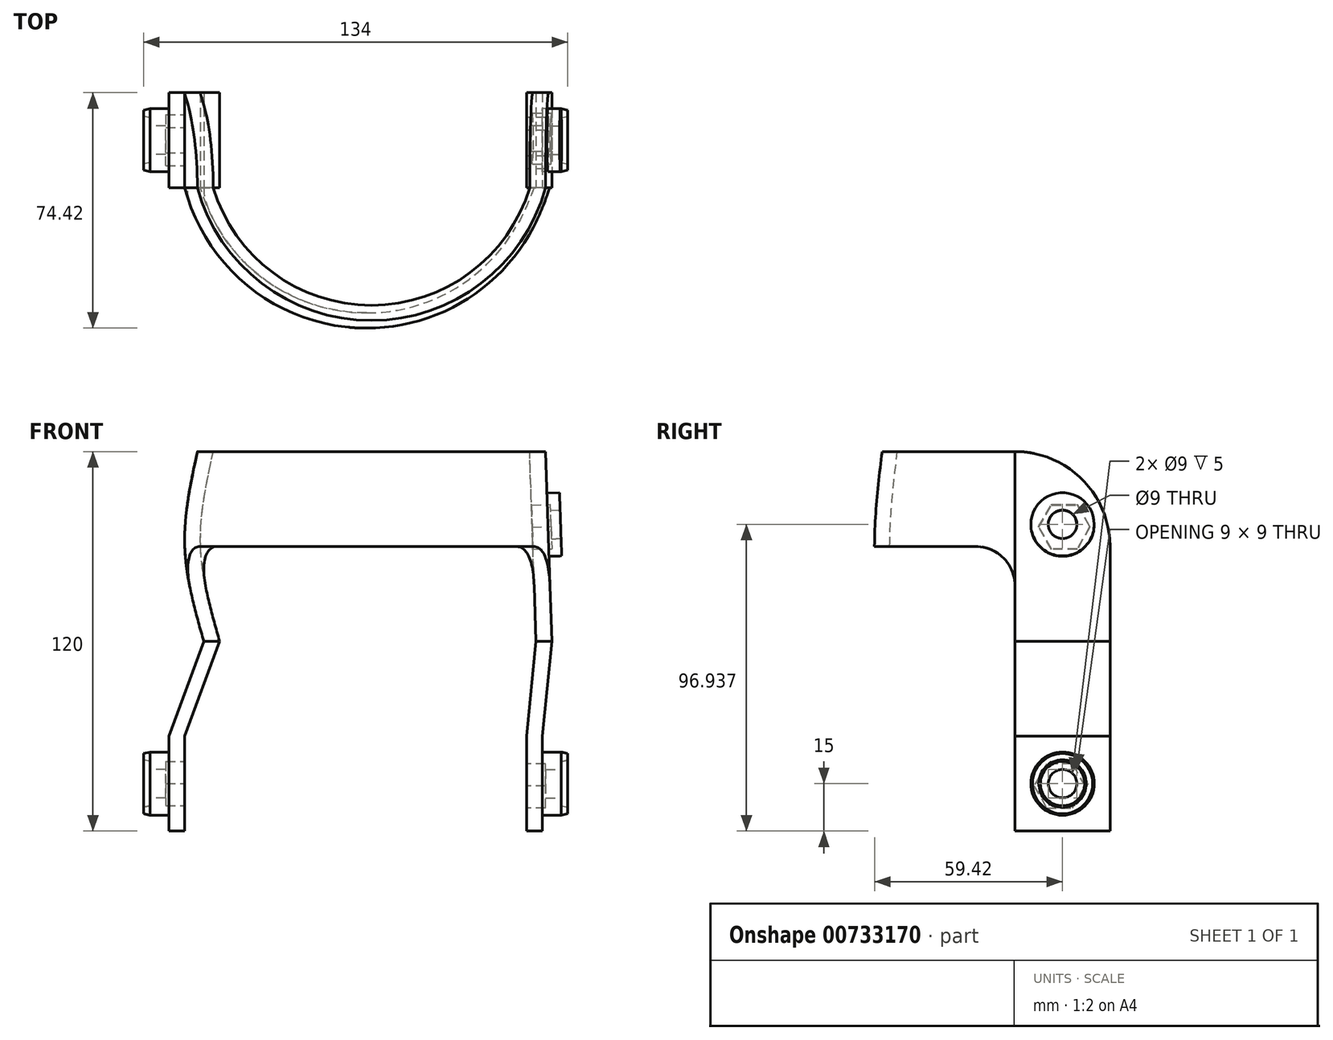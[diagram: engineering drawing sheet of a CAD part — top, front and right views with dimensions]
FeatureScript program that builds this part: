
annotation { "Feature Type Name" : "Feature", "Feature Type Description" : "" }
export const myFeature = defineFeature(function(context is Context, id is Id, definition is map)
    precondition{}
    {
        {
            var Q0;
            Q0=qCreatedBy(makeId("Top.planeOp"),FACE);
            var sketch = newSketch(context, id + "F0", { "sketchPlane" : qUnion([Q0])});
            skPoint(sketch, "E0", {"position": v(-54, 0) * mm});
            skPoint(sketch, "E1", {"position": v(0, 0) * mm});
            skPoint(sketch, "E2", {"position": v(54, 0) * mm});
            skPoint(sketch, "E3", {"position": v(-54, 15) * mm});
            skPoint(sketch, "E4", {"position": v(54, 15) * mm});
            skLineSegment(sketch, "E5.bottom", {"start": v(-54, 15) * mm, "end": v(-59, 15) * mm});
            skLineSegment(sketch, "E5.left", {"start": v(-54, 15) * mm, "end": v(-54, -15) * mm});
            skLineSegment(sketch, "E5.right", {"start": v(-59, 15) * mm, "end": v(-59, -15) * mm});
            skLineSegment(sketch, "E6.bottom", {"start": v(54, 15) * mm, "end": v(59, 15) * mm});
            skLineSegment(sketch, "E6.left", {"start": v(54, 15) * mm, "end": v(54, -15) * mm});
            skLineSegment(sketch, "E6.right", {"start": v(59, 15) * mm, "end": v(59, -15) * mm});
            skArc(sketch, "E7", {"start": v(-54, -15) * mm, "mid": v(0, -56.04) * mm, "end": v(54, -15) * mm});
            skArc(sketch, "E8", {"start": v(-59, -15) * mm, "mid": v(0, -60.88) * mm, "end": v(59, -15) * mm});
            skSolve(sketch);
        }
        {
            var Q0;
            Q0=qCreatedBy(makeId("Top.planeOp"),FACE);
            cPlane(context, id + "F1", {"entities" : qUnion([Q0]), "cplaneType" : CPlaneType.OFFSET, "offset" : 30 * mm, "width" : 150 * mm, "height" : 150 * mm});
        }
        {
            var Q0;
            Q0=qCreatedBy(id+"F1.planeOp",FACE);
            var sketch = newSketch(context, id + "F2", { "sketchPlane" : qUnion([Q0])});
            skPoint(sketch, "E9", {"position": v(-54, 0) * mm});
            skPoint(sketch, "E10", {"position": v(0, 0) * mm});
            skPoint(sketch, "E11", {"position": v(54, 0) * mm});
            skPoint(sketch, "E12", {"position": v(-54, 15) * mm});
            skPoint(sketch, "E13", {"position": v(54, 15) * mm});
            skLineSegment(sketch, "E14.bottom", {"start": v(-54, 15) * mm, "end": v(-59, 15) * mm});
            skLineSegment(sketch, "E14.left", {"start": v(-54, 15) * mm, "end": v(-54, -15) * mm});
            skLineSegment(sketch, "E14.right", {"start": v(-59, 15) * mm, "end": v(-59, -15) * mm});
            skLineSegment(sketch, "E15.bottom", {"start": v(54, 15) * mm, "end": v(59, 15) * mm});
            skLineSegment(sketch, "E15.left", {"start": v(54, 15) * mm, "end": v(54, -15) * mm});
            skLineSegment(sketch, "E15.right", {"start": v(59, 15) * mm, "end": v(59, -15) * mm});
            skArc(sketch, "E16", {"start": v(-54, -15) * mm, "mid": v(0, -56.04) * mm, "end": v(54, -15) * mm});
            skArc(sketch, "E17", {"start": v(-59, -15) * mm, "mid": v(0, -60.88) * mm, "end": v(59, -15) * mm});
            skSolve(sketch);
        }
        {
            var Q0;
            Q0=makeQuery(id+"F0.imprint","IMPRINT",FACE,{"disambiguationData":[TD([[makeQuery(id+"F0.imprint","IMPRINT",EDGE,{"derivedFrom":sQuery(id+"F0.wireOp",EDGE,"E5.bottom")}),1.0]])]});
            var Q1;
            Q1=makeQuery(id+"F2.imprint","IMPRINT",FACE,{"disambiguationData":[TD([[makeQuery(id+"F2.imprint","IMPRINT",EDGE,{"derivedFrom":sQuery(id+"F2.wireOp",EDGE,"E14.bottom")}),1.0]])]});
            loft(context, id + "F3", {"sheetProfilesArray" : [{ "sheetProfileEntities" : qUnion([Q0]) }, { "sheetProfileEntities" : qUnion([Q1]) }]});
        }
        {
            var Q0;
            Q0=qCreatedBy(makeId("Right.planeOp"),FACE);
            var sketch = newSketch(context, id + "F4", { "sketchPlane" : qUnion([Q0])});
            skPoint(sketch, "E18", {"position": v(-15, 0) * mm});
            skPoint(sketch, "E19", {"position": v(-15, 30) * mm});
            skLineSegment(sketch, "E20", {"start": v(-15, 30) * mm, "end": v(-15, 0) * mm});
            skLineSegment(sketch, "E21", {"start": v(-15, 30) * mm, "end": v(-100.5, 30) * mm});
            skLineSegment(sketch, "E22", {"start": v(-100.5, 30) * mm, "end": v(-100.5, 0) * mm});
            skLineSegment(sketch, "E23", {"start": v(-100.5, 0) * mm, "end": v(-15, 0) * mm});
            skSolve(sketch);
        }
        {
            var Q0;
            Q0 = qSketchRegion(id + "F4", true);
            extrude(context, id + "F5", {"entities" : qUnion([Q0]), "operationType" : NewBodyOperationType.REMOVE, "oppositeDirection" : true, "depth" : 100 * mm, "offsetDistance" : 25 * mm});
        }
        {
            var Q0;
            Q0 = qSketchRegion(id + "F4", true);
            extrude(context, id + "F6", {"entities" : qUnion([Q0]), "operationType" : NewBodyOperationType.REMOVE, "depth" : 100 * mm, "offsetDistance" : 25 * mm});
        }
        {
            var Q0;
            Q0=makeQuery(id+"F3.opLoft","SWEPT_FACE",FACE,{"disambiguationData":[OSD([sQuery(id+"F0.wireOp",EDGE,"E5.bottom"),sQuery(id+"F0.wireOp",EDGE,"E5.right"),sQuery(id+"F0.wireOp",EDGE,"E8"),sQuery(id+"F2.wireOp",EDGE,"E14.bottom"),sQuery(id+"F2.wireOp",EDGE,"E14.right"),sQuery(id+"F2.wireOp",EDGE,"E17")])]});
            var sketch = newSketch(context, id + "F7", { "sketchPlane" : qUnion([Q0])});
            skPoint(sketch, "E24", {"position": v(0, 15) * mm});
            skCircle(sketch, "E25", {"center": v(0, 15) * mm, "radius": 10 * mm});
            skSolve(sketch);
        }
        {
            var Q0;
            Q0=makeQuery(id+"F7.imprint","IMPRINT",FACE,{"disambiguationData":[TD([[makeQuery(id+"F7.imprint","IMPRINT",EDGE,{"derivedFrom":sQuery(id+"F7.wireOp",EDGE,"E25")}),1.0]])]});
            extrude(context, id + "F8", {"entities" : qUnion([Q0]), "operationType" : NewBodyOperationType.ADD, "depth" : 6 * mm, "offsetDistance" : 25 * mm});
        }
        {
            var Q0;
            Q0=makeQuery(id+"F3.opLoft","SWEPT_FACE",FACE,{"disambiguationData":[OSD([sQuery(id+"F0.wireOp",EDGE,"E5.bottom"),sQuery(id+"F0.wireOp",EDGE,"E5.left"),sQuery(id+"F0.wireOp",EDGE,"E5.right"),sQuery(id+"F2.wireOp",EDGE,"E14.bottom"),sQuery(id+"F2.wireOp",EDGE,"E14.left"),sQuery(id+"F2.wireOp",EDGE,"E14.right")])]});
            cPlane(context, id + "F9", {"entities" : qUnion([Q0]), "cplaneType" : CPlaneType.OFFSET, "offset" : 15 * mm, "oppositeDirection" : true, "width" : 150 * mm, "height" : 150 * mm});
        }
        {
            var Q0;
            Q0=qCreatedBy(id+"F9.planeOp",FACE);
            var sketch = newSketch(context, id + "F10", { "sketchPlane" : qUnion([Q0])});
            skPoint(sketch, "E26", {"position": v(54, 15) * mm});
            skPoint(sketch, "E27", {"position": v(34.48, 7.7) * mm});
            skPoint(sketch, "E28", {"position": v(65, 15) * mm});
            skLineSegment(sketch, "E29", {"start": v(65, 8) * mm, "end": v(65, 5) * mm});
            skLineSegment(sketch, "E30", {"start": v(65, 5) * mm, "end": v(67, 5.5) * mm});
            skLineSegment(sketch, "E31", {"start": v(67, 5.5) * mm, "end": v(67, 7.5) * mm});
            skLineSegment(sketch, "E32", {"start": v(67, 7.5) * mm, "end": v(65, 8) * mm});
            skPoint(sketch, "E33", {"position": v(65, 6.5) * mm});
            skPoint(sketch, "E34", {"position": v(67, 6.5) * mm});
            skLineSegment(sketch, "E35", {"start": v(65, 15) * mm, "end": v(67, 15) * mm});
            skLineSegment(sketch, "E36", {"start": v(65, 8) * mm, "end": v(67, 7.5) * mm});
            skLineSegment(sketch, "E37", {"start": v(67, 7.5) * mm, "end": v(67, 5.5) * mm});
            skLineSegment(sketch, "E38", {"start": v(67, 5.5) * mm, "end": v(65, 5) * mm});
            skLineSegment(sketch, "E39", {"start": v(65, 5) * mm, "end": v(65, 8) * mm});
            skPoint(sketch, "E40", {"position": v(59, 15) * mm});
            skSolve(sketch);
        }
        {
            var Q0;
            Q0 = qSketchRegion(id + "F10", true);
            var Q1;
            Q1=sQuery(id+"F10.wireOp",EDGE,"E35");
            revolve(context, id + "F11", {"operationType" : NewBodyOperationType.ADD, "surfaceOperationType" : NewSurfaceOperationType.NEW, "entities" : qUnion([Q0]), "axis" : qUnion([Q1]), "revolveType" : RevolveType.FULL});
        }
        {
            var Q0;
            Q0=makeQuery(id+"F8.opExtrude","CAP_FACE",FACE,{"disambiguationData":[OSD([sQuery(id+"F7.wireOp",EDGE,"E25")])],"isStart":false});
            var sketch = newSketch(context, id + "F12", { "sketchPlane" : qUnion([Q0])});
            skPoint(sketch, "E41", {"position": v(0, 15) * mm});
            skCircle(sketch, "E42", {"center": v(0, 15) * mm, "radius": 4.5 * mm});
            skSolve(sketch);
        }
        {
            var Q0;
            Q0=makeQuery(id+"F12.imprint","IMPRINT",FACE,{"disambiguationData":[TD([[makeQuery(id+"F12.imprint","IMPRINT",EDGE,{"derivedFrom":sQuery(id+"F12.wireOp",EDGE,"E42")}),1.0]])]});
            extrude(context, id + "F13", {"entities" : qUnion([Q0]), "operationType" : NewBodyOperationType.REMOVE, "oppositeDirection" : true, "depth" : 25 * mm, "offsetDistance" : 25 * mm});
        }
        {
            var Q0;
            Q0=makeQuery(id+"F3.opLoft","SWEPT_FACE",FACE,{"disambiguationData":[OSD([sQuery(id+"F0.wireOp",EDGE,"E5.bottom"),sQuery(id+"F0.wireOp",EDGE,"E5.left"),sQuery(id+"F0.wireOp",EDGE,"E7"),sQuery(id+"F2.wireOp",EDGE,"E14.bottom"),sQuery(id+"F2.wireOp",EDGE,"E14.left"),sQuery(id+"F2.wireOp",EDGE,"E16")])]});
            var sketch = newSketch(context, id + "F14", { "sketchPlane" : qUnion([Q0])});
            skPoint(sketch, "E43", {"position": v(0, 15) * mm});
            skCircle(sketch, "E44", {"center": v(0, 15) * mm, "radius": 7 * mm});
            skPoint(sketch, "E45", {"position": v(0, 22) * mm});
            skCircle(sketch, "E46.cCircle", {"center": v(0, 15) * mm, "radius": 7 * mm, "construction": true});
            skLineSegment(sketch, "E46.0", {"start": v(-4.04, 22) * mm, "end": v(4.04, 22) * mm});
            skLineSegment(sketch, "E46.1", {"start": v(4.04, 22) * mm, "end": v(8.08, 15) * mm});
            skLineSegment(sketch, "E46.2", {"start": v(8.08, 15) * mm, "end": v(4.04, 8) * mm});
            skLineSegment(sketch, "E46.3", {"start": v(4.04, 8) * mm, "end": v(-4.04, 8) * mm});
            skLineSegment(sketch, "E46.4", {"start": v(-4.04, 8) * mm, "end": v(-8.08, 15) * mm});
            skLineSegment(sketch, "E46.5", {"start": v(-8.08, 15) * mm, "end": v(-4.04, 22) * mm});
            skSolve(sketch);
        }
        {
            var Q0;
            Q0 = qSketchRegion(id + "F14", true);
            extrude(context, id + "F15", {"entities" : qUnion([Q0]), "operationType" : NewBodyOperationType.REMOVE, "oppositeDirection" : true, "depth" : 6 * mm, "offsetDistance" : 25 * mm});
        }
        {
            var Q0;
            Q0=makeQuery(id+"F3.opLoft","SWEPT_FACE",FACE,{"disambiguationData":[OSD([sQuery(id+"F0.wireOp",EDGE,"E6.bottom"),sQuery(id+"F0.wireOp",EDGE,"E6.right"),sQuery(id+"F0.wireOp",EDGE,"E8"),sQuery(id+"F2.wireOp",EDGE,"E15.bottom"),sQuery(id+"F2.wireOp",EDGE,"E15.right"),sQuery(id+"F2.wireOp",EDGE,"E17")])]});
            var sketch = newSketch(context, id + "F16", { "sketchPlane" : qUnion([Q0])});
            skPoint(sketch, "E47", {"position": v(0, 15) * mm});
            skCircle(sketch, "E48", {"center": v(0, 15) * mm, "radius": 10 * mm});
            skSolve(sketch);
        }
        {
            var Q0;
            Q0 = qSketchRegion(id + "F16", true);
            extrude(context, id + "F17", {"entities" : qUnion([Q0]), "operationType" : NewBodyOperationType.ADD, "depth" : 6 * mm, "offsetDistance" : 25 * mm});
        }
        {
            var Q0;
            Q0=qCreatedBy(id+"F9.planeOp",FACE);
            var sketch = newSketch(context, id + "F18", { "sketchPlane" : qUnion([Q0])});
            skPoint(sketch, "E49", {"position": v(-54, 15) * mm});
            skPoint(sketch, "E50", {"position": v(-34.79, 13.98) * mm});
            skPoint(sketch, "E51", {"position": v(-65, 15) * mm});
            skLineSegment(sketch, "E52", {"start": v(-65, 22) * mm, "end": v(-65, 25) * mm});
            skLineSegment(sketch, "E53", {"start": v(-65, 25) * mm, "end": v(-67, 24.5) * mm});
            skLineSegment(sketch, "E54", {"start": v(-67, 24.5) * mm, "end": v(-67, 22.5) * mm});
            skLineSegment(sketch, "E55", {"start": v(-67, 22.5) * mm, "end": v(-65, 22) * mm});
            skPoint(sketch, "E56", {"position": v(-65, 23.5) * mm});
            skPoint(sketch, "E57", {"position": v(-67, 23.5) * mm});
            skLineSegment(sketch, "E58", {"start": v(-65, 15) * mm, "end": v(-67, 15) * mm});
            skLineSegment(sketch, "E59", {"start": v(-65, 22) * mm, "end": v(-67, 22.5) * mm});
            skLineSegment(sketch, "E60", {"start": v(-67, 22.5) * mm, "end": v(-67, 24.5) * mm});
            skLineSegment(sketch, "E61", {"start": v(-67, 24.5) * mm, "end": v(-65, 25) * mm});
            skLineSegment(sketch, "E62", {"start": v(-65, 25) * mm, "end": v(-65, 22) * mm});
            skPoint(sketch, "E63", {"position": v(-45.27, 16.08) * mm});
            skSolve(sketch);
        }
        {
            var Q0;
            Q0 = qSketchRegion(id + "F18", true);
            var Q1;
            Q1=sQuery(id+"F18.wireOp",EDGE,"E58");
            revolve(context, id + "F19", {"operationType" : NewBodyOperationType.ADD, "surfaceOperationType" : NewSurfaceOperationType.NEW, "entities" : qUnion([Q0]), "axis" : qUnion([Q1]), "revolveType" : RevolveType.FULL});
        }
        {
            var Q0;
            Q0=makeQuery(id+"F17.opExtrude","CAP_FACE",FACE,{"disambiguationData":[OSD([sQuery(id+"F16.wireOp",EDGE,"E48")])],"isStart":false});
            var sketch = newSketch(context, id + "F20", { "sketchPlane" : qUnion([Q0])});
            skPoint(sketch, "E64", {"position": v(0, 15) * mm});
            skCircle(sketch, "E65", {"center": v(0, 15) * mm, "radius": 4.5 * mm});
            skSolve(sketch);
        }
        {
            var Q0;
            Q0 = qSketchRegion(id + "F20", true);
            extrude(context, id + "F21", {"entities" : qUnion([Q0]), "operationType" : NewBodyOperationType.REMOVE, "oppositeDirection" : true, "depth" : 30 * mm, "offsetDistance" : 25 * mm});
        }
        {
            var Q0;
            Q0=makeQuery(id+"F3.opLoft","SWEPT_FACE",FACE,{"disambiguationData":[OSD([sQuery(id+"F0.wireOp",EDGE,"E6.bottom"),sQuery(id+"F0.wireOp",EDGE,"E6.left"),sQuery(id+"F0.wireOp",EDGE,"E7"),sQuery(id+"F2.wireOp",EDGE,"E15.bottom"),sQuery(id+"F2.wireOp",EDGE,"E15.left"),sQuery(id+"F2.wireOp",EDGE,"E16")])]});
            var sketch = newSketch(context, id + "F22", { "sketchPlane" : qUnion([Q0])});
            skPoint(sketch, "E66", {"position": v(0, 15) * mm});
            skPoint(sketch, "E67", {"position": v(0.93, 14.27) * mm});
            skCircle(sketch, "E68", {"center": v(0.93, 14.27) * mm, "radius": 7 * mm});
            skPoint(sketch, "E69", {"position": v(0.93, 21.27) * mm});
            skCircle(sketch, "E70.cCircle", {"center": v(0.93, 14.27) * mm, "radius": 7 * mm, "construction": true});
            skLineSegment(sketch, "E70.0", {"start": v(-3.11, 21.27) * mm, "end": v(4.97, 21.27) * mm});
            skLineSegment(sketch, "E70.1", {"start": v(4.97, 21.27) * mm, "end": v(9.01, 14.27) * mm});
            skLineSegment(sketch, "E70.2", {"start": v(9.01, 14.27) * mm, "end": v(4.97, 7.27) * mm});
            skLineSegment(sketch, "E70.3", {"start": v(4.97, 7.27) * mm, "end": v(-3.11, 7.27) * mm});
            skLineSegment(sketch, "E70.4", {"start": v(-3.11, 7.27) * mm, "end": v(-7.15, 14.27) * mm});
            skLineSegment(sketch, "E70.5", {"start": v(-7.15, 14.27) * mm, "end": v(-3.11, 21.27) * mm});
            skSolve(sketch);
        }
        {
            var Q0;
            Q0 = qSketchRegion(id + "F22", true);
            extrude(context, id + "F23", {"entities" : qUnion([Q0]), "operationType" : NewBodyOperationType.REMOVE, "oppositeDirection" : true, "depth" : 6 * mm, "offsetDistance" : 25 * mm});
        }
        {
            var Q0;
            Q0=qCreatedBy(makeId("Top.planeOp"),FACE);
            cPlane(context, id + "F24", {"entities" : qUnion([Q0]), "cplaneType" : CPlaneType.OFFSET, "offset" : 60 * mm, "width" : 150 * mm, "height" : 150 * mm});
        }
        {
            var Q0;
            Q0=qCreatedBy(id+"F24.planeOp",FACE);
            var sketch = newSketch(context, id + "F25", { "sketchPlane" : qUnion([Q0])});
            skPoint(sketch, "E71", {"position": v(7, 0) * mm});
            skLineSegment(sketch, "E72", {"start": v(-43, 7.11) * mm, "end": v(-43, 15) * mm});
            skLineSegment(sketch, "E73", {"start": v(-48, 15) * mm, "end": v(-48, -15) * mm});
            skLineSegment(sketch, "E74", {"start": v(-43, -15) * mm, "end": v(-43, 7.11) * mm});
            skLineSegment(sketch, "E75", {"start": v(57, 7.11) * mm, "end": v(57, 15) * mm});
            skLineSegment(sketch, "E76", {"start": v(62, 15) * mm, "end": v(62, -15) * mm});
            skLineSegment(sketch, "E77", {"start": v(57, -15) * mm, "end": v(57, 7.11) * mm});
            skLineSegment(sketch, "E78", {"start": v(-48, 15) * mm, "end": v(-43, 15) * mm});
            skLineSegment(sketch, "E79", {"start": v(57, 15) * mm, "end": v(62, 15) * mm});
            skArc(sketch, "E80", {"start": v(-43, -15) * mm, "mid": v(7, -52.2) * mm, "end": v(57, -15) * mm});
            skArc(sketch, "E81", {"start": v(-48, -15) * mm, "mid": v(7, -57) * mm, "end": v(62, -15) * mm});
            skPoint(sketch, "E82", {"position": v(7, -52.2) * mm});
            skPoint(sketch, "E83", {"position": v(7, -57) * mm});
            skPoint(sketch, "E84", {"position": v(-43, 7.11) * mm});
            skSolve(sketch);
        }
        {
            var Q0;
            Q0=qCreatedBy(makeId("Top.planeOp"),FACE);
            cPlane(context, id + "F26", {"entities" : qUnion([Q0]), "cplaneType" : CPlaneType.OFFSET, "offset" : 90 * mm, "width" : 150 * mm, "height" : 150 * mm});
        }
        {
            var Q0;
            Q0=qCreatedBy(id+"F26.planeOp",FACE);
            var sketch = newSketch(context, id + "F27", { "sketchPlane" : qUnion([Q0])});
            skPoint(sketch, "E85", {"position": v(3.5, 0) * mm});
            skLineSegment(sketch, "E86", {"start": v(3.5, 0) * mm, "end": v(56, 0) * mm});
            skLineSegment(sketch, "E87", {"start": v(-49, 0) * mm, "end": v(-49, 15) * mm});
            skLineSegment(sketch, "E88", {"start": v(-54, 15) * mm, "end": v(-54, -15) * mm});
            skLineSegment(sketch, "E89", {"start": v(-49, -15) * mm, "end": v(-49, 0) * mm});
            skLineSegment(sketch, "E90", {"start": v(56, 0) * mm, "end": v(56, 15) * mm});
            skLineSegment(sketch, "E91", {"start": v(61, 15) * mm, "end": v(61, -15) * mm});
            skLineSegment(sketch, "E92", {"start": v(56, -15) * mm, "end": v(56, 0) * mm});
            skLineSegment(sketch, "E93", {"start": v(-54, 15) * mm, "end": v(-49, 15) * mm});
            skLineSegment(sketch, "E94", {"start": v(56, 15) * mm, "end": v(61, 15) * mm});
            skArc(sketch, "E95", {"start": v(-49, -15) * mm, "mid": v(3.5, -54.6) * mm, "end": v(56, -15) * mm});
            skArc(sketch, "E96", {"start": v(61, -15) * mm, "mid": v(3.5, -59.42) * mm, "end": v(-54, -15) * mm});
            skPoint(sketch, "E97", {"position": v(3.5, -54.6) * mm});
            skPoint(sketch, "E98", {"position": v(3.5, -59.42) * mm});
            skSolve(sketch);
        }
        {
            var Q0;
            Q0=qCreatedBy(makeId("Top.planeOp"),FACE);
            cPlane(context, id + "F28", {"entities" : qUnion([Q0]), "cplaneType" : CPlaneType.OFFSET, "offset" : 120 * mm, "width" : 150 * mm, "height" : 150 * mm});
        }
        {
            var Q0;
            Q0=qCreatedBy(id+"F28.planeOp",FACE);
            var sketch = newSketch(context, id + "F29", { "sketchPlane" : qUnion([Q0])});
            skPoint(sketch, "E99", {"position": v(5, 0) * mm});
            skLineSegment(sketch, "E100", {"start": v(55, 0) * mm, "end": v(55, 15) * mm});
            skLineSegment(sketch, "E101", {"start": v(60, 15) * mm, "end": v(60, -15) * mm});
            skLineSegment(sketch, "E102", {"start": v(55, -15) * mm, "end": v(55, 0) * mm});
            skLineSegment(sketch, "E103", {"start": v(-45, 0) * mm, "end": v(-45, 15) * mm});
            skLineSegment(sketch, "E104", {"start": v(-50, 15) * mm, "end": v(-50, -15) * mm});
            skLineSegment(sketch, "E105", {"start": v(-45, -15) * mm, "end": v(-45, 0) * mm});
            skLineSegment(sketch, "E106", {"start": v(-50, 15) * mm, "end": v(-45, 15) * mm});
            skLineSegment(sketch, "E107", {"start": v(55, 15) * mm, "end": v(60, 15) * mm});
            skArc(sketch, "E108", {"start": v(-45, -15) * mm, "mid": v(5, -52.2) * mm, "end": v(55, -15) * mm});
            skArc(sketch, "E109", {"start": v(60, -15) * mm, "mid": v(5, -57) * mm, "end": v(-50, -15) * mm});
            skPoint(sketch, "E110", {"position": v(5, -52.2) * mm});
            skPoint(sketch, "E111", {"position": v(5, -57) * mm});
            skSolve(sketch);
        }
        {
            var Q0;
            Q0=qCreatedBy(id+"F24.planeOp",FACE);
            var sketch = newSketch(context, id + "F30", { "sketchPlane" : qUnion([Q0])});
            skPoint(sketch, "E112", {"position": v(0, 15) * mm});
            skPoint(sketch, "E113", {"position": v(57, -15) * mm});
            skPoint(sketch, "E114", {"position": v(62, -15) * mm});
            skPoint(sketch, "E115", {"position": v(-17.28, 15) * mm});
            skPoint(sketch, "E116", {"position": v(62, 15) * mm});
            skPoint(sketch, "E117", {"position": v(57, 15) * mm});
            skLineSegment(sketch, "E118", {"start": v(57, 15) * mm, "end": v(62, 15) * mm});
            skLineSegment(sketch, "E119", {"start": v(62, -15) * mm, "end": v(57, -15) * mm});
            skLineSegment(sketch, "E120", {"start": v(57, 15) * mm, "end": v(57, -15) * mm});
            skLineSegment(sketch, "E121", {"start": v(62, 15) * mm, "end": v(62, -15) * mm});
            skSolve(sketch);
        }
        {
            var Q0;
            {var subQ2=sQuery(id+"F2.wireOp",EDGE,"E14.bottom");Q0=makeQuery(id+"F5.boolean.opBoolean","SPLIT",FACE,{"disambiguationData":[TD([makeQuery(id+"F5.opExtrude","SWEPT_FACE",FACE,{"disambiguationData":[OSD([sQuery(id+"F4.wireOp",EDGE,"E20")])]})])],"derivedFrom":makeQuery(id+"F3.opLoft","CAP_FACE",FACE,{"disambiguationData":[OSD([makeQuery(id+"F2.imprint","IMPRINT",FACE,{"disambiguationData":[TD([[makeQuery(id+"F2.imprint","IMPRINT",EDGE,{"derivedFrom":subQ2}),1.0]])]})])],"isStart":true})});}
            var sketch = newSketch(context, id + "F31", { "sketchPlane" : qUnion([Q0])});
            skPoint(sketch, "E122", {"position": v(59, -15) * mm});
            skPoint(sketch, "E123", {"position": v(59, 15) * mm});
            skPoint(sketch, "E124", {"position": v(54, 15) * mm});
            skPoint(sketch, "E125", {"position": v(54, -15) * mm});
            skLineSegment(sketch, "E126", {"start": v(54, 15) * mm, "end": v(59, 15) * mm});
            skLineSegment(sketch, "E127", {"start": v(59, -15) * mm, "end": v(54, -15) * mm});
            skLineSegment(sketch, "E128", {"start": v(54, 15) * mm, "end": v(54, -15) * mm});
            skLineSegment(sketch, "E129", {"start": v(59, 15) * mm, "end": v(59, -15) * mm});
            skSolve(sketch);
        }
        {
            var Q1;
            Q1 = qSketchRegion(id + "F31", true);
            var Q2;
            Q2 = qSketchRegion(id + "F30", true);
            loft(context, id + "F32", {"operationType" : NewBodyOperationType.ADD, "sheetProfilesArray" : [{ "sheetProfileEntities" : qUnion([Q1]) }, { "sheetProfileEntities" : qUnion([Q2]) }]});
        }
        {
            var Q0;
            Q0=qCreatedBy(id+"F24.planeOp",FACE);
            var sketch = newSketch(context, id + "F33", { "sketchPlane" : qUnion([Q0])});
            skPoint(sketch, "E130", {"position": v(-48, -15) * mm});
            skPoint(sketch, "E131", {"position": v(-48, 15) * mm});
            skPoint(sketch, "E132", {"position": v(-43, 15) * mm});
            skPoint(sketch, "E133", {"position": v(-43, -15) * mm});
            skLineSegment(sketch, "E134", {"start": v(-48, 15) * mm, "end": v(-43, 15) * mm});
            skLineSegment(sketch, "E135", {"start": v(-43, -15) * mm, "end": v(-48, -15) * mm});
            skLineSegment(sketch, "E136", {"start": v(-48, 15) * mm, "end": v(-48, -18.48) * mm});
            skLineSegment(sketch, "E137", {"start": v(-43, 15) * mm, "end": v(-43, -15) * mm});
            skSolve(sketch);
        }
        {
            var Q0;
            {var subQ2=sQuery(id+"F2.wireOp",EDGE,"E14.bottom");Q0=makeQuery(id+"F5.boolean.opBoolean","SPLIT",FACE,{"disambiguationData":[TD([makeQuery(id+"F5.opExtrude","SWEPT_FACE",FACE,{"disambiguationData":[OSD([sQuery(id+"F4.wireOp",EDGE,"E20")])]})])],"derivedFrom":makeQuery(id+"F3.opLoft","CAP_FACE",FACE,{"disambiguationData":[OSD([makeQuery(id+"F2.imprint","IMPRINT",FACE,{"disambiguationData":[TD([[makeQuery(id+"F2.imprint","IMPRINT",EDGE,{"derivedFrom":subQ2}),1.0]])]})])],"isStart":true})});}
            var sketch = newSketch(context, id + "F34", { "sketchPlane" : qUnion([Q0])});
            skLineSegment(sketch, "E138", {"start": v(-59, -15) * mm, "end": v(-54, -15) * mm});
            skLineSegment(sketch, "E139", {"start": v(-54, -15) * mm, "end": v(-54, 15) * mm});
            skLineSegment(sketch, "E140", {"start": v(-54, 15) * mm, "end": v(-59, 15) * mm});
            skLineSegment(sketch, "E141", {"start": v(-59, 15) * mm, "end": v(-59, -15) * mm});
            skSolve(sketch);
        }
        {
            var Q1;
            Q1 = qSketchRegion(id + "F33", true);
            var Q2;
            Q2 = qSketchRegion(id + "F34", true);
            loft(context, id + "F35", {"operationType" : NewBodyOperationType.ADD, "sheetProfilesArray" : [{ "sheetProfileEntities" : qUnion([Q1]) }, { "sheetProfileEntities" : qUnion([Q2]) }]});
        }
        {
            var Q0;
            Q0=makeQuery(id+"F25.imprint","IMPRINT",FACE,{"disambiguationData":[TD([[makeQuery(id+"F25.imprint","IMPRINT",EDGE,{"derivedFrom":sQuery(id+"F25.wireOp",EDGE,"E72")}),1.0]])]});
            var Q1;
            Q1=makeQuery(id+"F27.imprint","IMPRINT",FACE,{"disambiguationData":[TD([[makeQuery(id+"F27.imprint","IMPRINT",EDGE,{"derivedFrom":sQuery(id+"F27.wireOp",EDGE,"E87")}),1.0]])]});
            var Q2;
            Q2=makeQuery(id+"F29.imprint","IMPRINT",FACE,{"disambiguationData":[TD([[makeQuery(id+"F29.imprint","IMPRINT",EDGE,{"derivedFrom":sQuery(id+"F29.wireOp",EDGE,"E100")}),-1.0]])]});
            loft(context, id + "F36", {"sheetProfilesArray" : [{ "sheetProfileEntities" : qUnion([Q0]) }, { "sheetProfileEntities" : qUnion([Q1]) }, { "sheetProfileEntities" : qUnion([Q2]) }]});
        }
        {
            var Q0;
            Q0=qCreatedBy(makeId("Right.planeOp"),FACE);
            var sketch = newSketch(context, id + "F37", { "sketchPlane" : qUnion([Q0])});
            skPoint(sketch, "E142", {"position": v(15, 120) * mm});
            skPoint(sketch, "E143", {"position": v(67.72, 92.75) * mm});
            skPoint(sketch, "E144", {"position": v(-57, 120) * mm});
            skPoint(sketch, "E145", {"position": v(15, 89.84) * mm});
            skPoint(sketch, "E146", {"position": v(-15, 60) * mm});
            skPoint(sketch, "E147", {"position": v(-15, 90) * mm});
            skArc(sketch, "E148", {"start": v(15, 89.84) * mm, "mid": v(6.27, 111.16) * mm, "end": v(-15, 120) * mm});
            skPoint(sketch, "E149", {"position": v(-27.52, 77.48) * mm});
            skArc(sketch, "E150", {"start": v(-15, 77.48) * mm, "mid": v(-18.67, 86.33) * mm, "end": v(-27.52, 90) * mm});
            skLineSegment(sketch, "E151", {"start": v(-27.52, 90) * mm, "end": v(-97.48, 90) * mm});
            skLineSegment(sketch, "E152", {"start": v(-97.48, 90) * mm, "end": v(-101.8, 120) * mm});
            skLineSegment(sketch, "E153", {"start": v(-101.8, 120) * mm, "end": v(-15, 120) * mm});
            skLineSegment(sketch, "E154", {"start": v(-15, 77.48) * mm, "end": v(-15, 32.67) * mm});
            skLineSegment(sketch, "E155", {"start": v(-15, 32.67) * mm, "end": v(-164.1, 32.67) * mm});
            skLineSegment(sketch, "E156", {"start": v(-164.1, 32.67) * mm, "end": v(-164.1, 138.62) * mm});
            skLineSegment(sketch, "E157", {"start": v(-164.1, 138.62) * mm, "end": v(15.89, 138.62) * mm});
            skLineSegment(sketch, "E158", {"start": v(15.89, 138.62) * mm, "end": v(15, 89.84) * mm});
            skSolve(sketch);
        }
        {
            var Q0;
            Q0 = qSketchRegion(id + "F37", true);
            extrude(context, id + "F38", {"entities" : qUnion([Q0]), "operationType" : NewBodyOperationType.REMOVE, "oppositeDirection" : true, "depth" : 100 * mm, "offsetDistance" : 25 * mm});
        }
        {
            var Q0;
            Q0 = qSketchRegion(id + "F37", true);
            extrude(context, id + "F39", {"entities" : qUnion([Q0]), "operationType" : NewBodyOperationType.REMOVE, "depth" : 100 * mm, "offsetDistance" : 25 * mm});
        }
        {
            var Q0;
            Q0=makeQuery(id+"F36.opLoft","SWEPT_FACE",FACE,{"disambiguationData":[OSD([sQuery(id+"F25.wireOp",EDGE,"E76"),sQuery(id+"F25.wireOp",EDGE,"E79"),sQuery(id+"F25.wireOp",EDGE,"E81"),sQuery(id+"F27.wireOp",EDGE,"E91"),sQuery(id+"F27.wireOp",EDGE,"E94"),sQuery(id+"F27.wireOp",EDGE,"E96")])]});
            var sketch = newSketch(context, id + "F40", { "sketchPlane" : qUnion([Q0])});
            skPoint(sketch, "E159", {"position": v(0, 94.78) * mm});
            skCircle(sketch, "E160", {"center": v(0, 94.78) * mm, "radius": 10 * mm});
            skSolve(sketch);
        }
        {
            var Q0;
            Q0 = qSketchRegion(id + "F40", true);
            extrude(context, id + "F41", {"entities" : qUnion([Q0]), "operationType" : NewBodyOperationType.ADD, "depth" : 4 * mm, "offsetDistance" : 25 * mm});
        }
        {
            var Q0;
            Q0=makeQuery(id+"F41.opExtrude","CAP_FACE",FACE,{"disambiguationData":[OSD([sQuery(id+"F40.wireOp",EDGE,"E160")])],"isStart":false});
            var sketch = newSketch(context, id + "F42", { "sketchPlane" : qUnion([Q0])});
            skPoint(sketch, "E161", {"position": v(0, 94.78) * mm});
            skCircle(sketch, "E162", {"center": v(0, 94.78) * mm, "radius": 4.5 * mm});
            skSolve(sketch);
        }
        {
            var Q0;
            Q0=makeQuery(id+"F41.opExtrude","CAP_FACE",FACE,{"disambiguationData":[OSD([sQuery(id+"F40.wireOp",EDGE,"E160")])],"isStart":false});
            var sketch = newSketch(context, id + "F43", { "sketchPlane" : qUnion([Q0])});
            skPoint(sketch, "E163", {"position": v(-4.97, 105.65) * mm});
            skPoint(sketch, "E164", {"position": v(-4.97, 87.6) * mm});
            skPoint(sketch, "E165", {"position": v(-29.72, 97.74) * mm});
            skPoint(sketch, "E166", {"position": v(0, 94.78) * mm});
            skPoint(sketch, "E167", {"position": v(-0.38, 94.87) * mm});
            skPoint(sketch, "E168", {"position": v(0.55, 94.14) * mm});
            skCircle(sketch, "E169", {"center": v(0.55, 94.14) * mm, "radius": 7 * mm});
            skPoint(sketch, "E170", {"position": v(0.55, 101.14) * mm});
            skCircle(sketch, "E171.cCircle", {"center": v(0.55, 94.14) * mm, "radius": 7 * mm, "construction": true});
            skLineSegment(sketch, "E171.0", {"start": v(-3.49, 101.14) * mm, "end": v(4.6, 101.14) * mm});
            skLineSegment(sketch, "E171.1", {"start": v(4.6, 101.14) * mm, "end": v(8.64, 94.14) * mm});
            skLineSegment(sketch, "E171.2", {"start": v(8.64, 94.14) * mm, "end": v(4.6, 87.14) * mm});
            skLineSegment(sketch, "E171.3", {"start": v(4.6, 87.14) * mm, "end": v(-3.49, 87.14) * mm});
            skLineSegment(sketch, "E171.4", {"start": v(-3.49, 87.14) * mm, "end": v(-7.53, 94.14) * mm});
            skLineSegment(sketch, "E171.5", {"start": v(-7.53, 94.14) * mm, "end": v(-3.49, 101.14) * mm});
            skSolve(sketch);
        }
        {
            var Q0;
            Q0=makeQuery(id+"F42.imprint","IMPRINT",FACE,{"disambiguationData":[TD([[makeQuery(id+"F42.imprint","IMPRINT",EDGE,{"derivedFrom":sQuery(id+"F42.wireOp",EDGE,"E162")}),1.0]])]});
            extrude(context, id + "F44", {"entities" : qUnion([Q0]), "operationType" : NewBodyOperationType.REMOVE, "oppositeDirection" : true, "depth" : 25 * mm, "offsetDistance" : 25 * mm});
        }
        {
            var Q0;
            Q0 = qSketchRegion(id + "F43", true);
            extrude(context, id + "F45", {"entities" : qUnion([Q0]), "operationType" : NewBodyOperationType.REMOVE, "oppositeDirection" : true, "depth" : 50 * mm, "offsetDistance" : 25 * mm, "hasSecondDirection" : true, "secondDirectionOppositeDirection" : true, "secondDirectionDepth" : 3 * mm});
        }
        {
            var Q0;
            Q0=makeQuery(id+"F36.opLoft","SWEPT_FACE",FACE,{"disambiguationData":[OSD([sQuery(id+"F25.wireOp",EDGE,"E75"),sQuery(id+"F25.wireOp",EDGE,"E77"),sQuery(id+"F25.wireOp",EDGE,"E79"),sQuery(id+"F27.wireOp",EDGE,"E90"),sQuery(id+"F27.wireOp",EDGE,"E92"),sQuery(id+"F27.wireOp",EDGE,"E94")])]});
            cPlane(context, id + "F46", {"entities" : qUnion([Q0]), "cplaneType" : CPlaneType.OFFSET, "offset" : 116 * mm, "width" : 150 * mm, "height" : 150 * mm});
        }
    });
